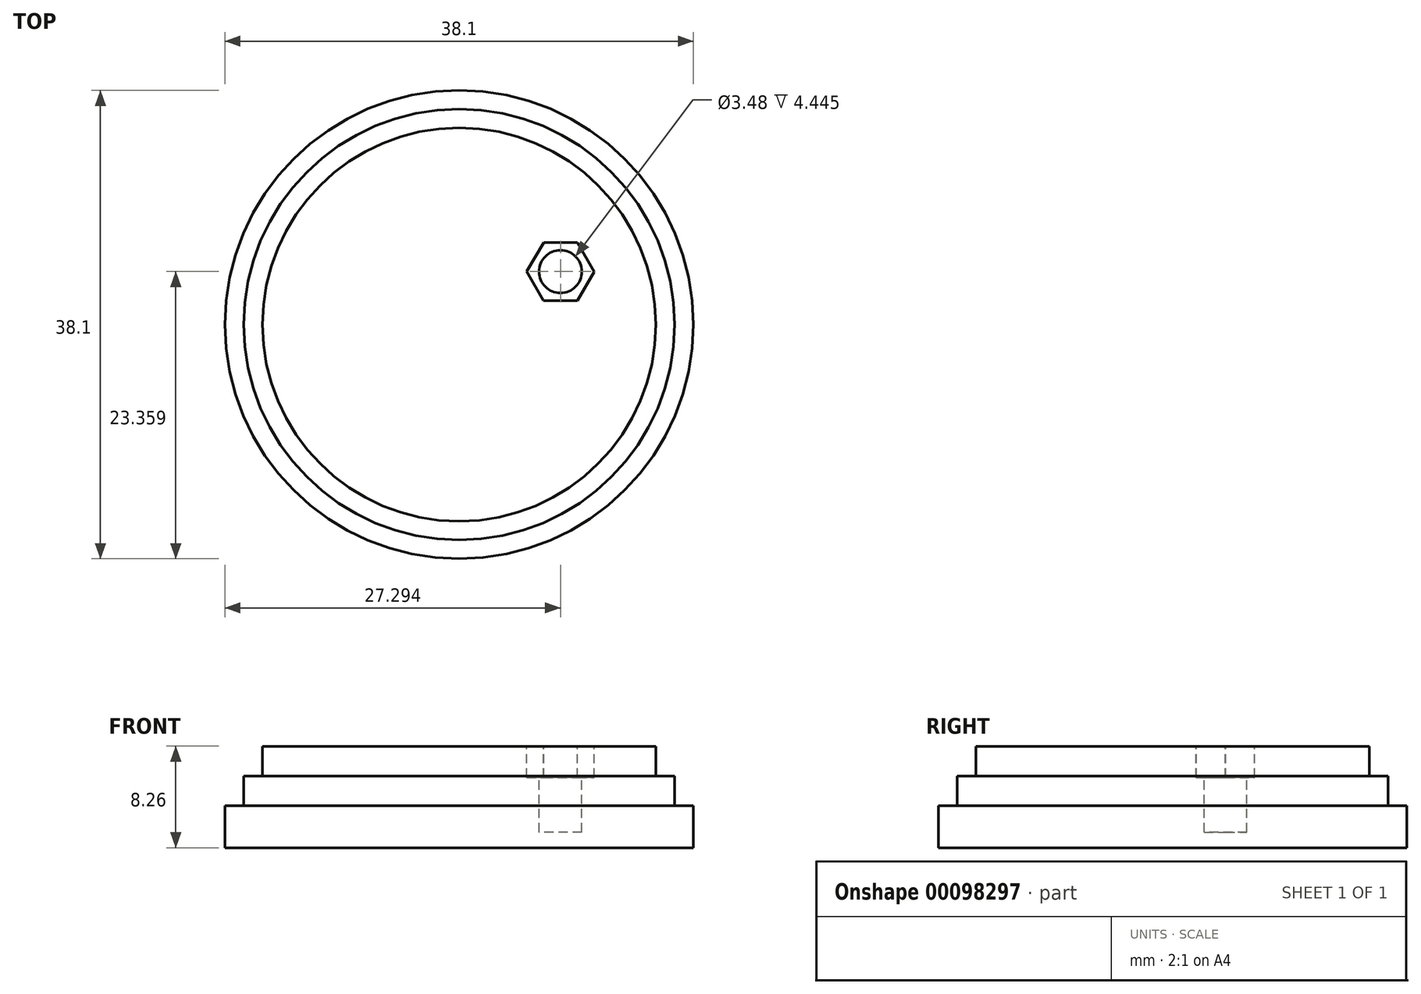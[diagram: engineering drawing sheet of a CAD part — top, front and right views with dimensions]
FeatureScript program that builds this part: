
annotation { "Feature Type Name" : "Feature", "Feature Type Description" : "" }
export const myFeature = defineFeature(function(context is Context, id is Id, definition is map)
    precondition{}
    {
        {
            var Q0;
            Q0=qCreatedBy(makeId("Front.planeOp"),FACE);
            var sketch = newSketch(context, id + "F0", { "sketchPlane" : qUnion([Q0])});
            skLineSegment(sketch, "E0", {"start": v(0, 0) * mm, "end": v(0, 3.43) * mm});
            skLineSegment(sketch, "E1", {"start": v(0, 3.43) * mm, "end": v(19.05, 3.43) * mm});
            skLineSegment(sketch, "E2", {"start": v(19.05, 3.43) * mm, "end": v(19.05, 0) * mm});
            skLineSegment(sketch, "E3", {"start": v(19.05, 0) * mm, "end": v(0, 0) * mm});
            skSolve(sketch);
        }
        {
            var Q0;
            Q0=qSketchRegion(id+"F0",true);
            var Q1;
            Q1=sQuery(id+"F0.wireOp",EDGE,"E0");
            revolve(context, id + "F1", {"entities" : qUnion([Q0]), "axis" : qUnion([Q1]), "revolveType" : RevolveType.FULL});
        }
        {
            var Q0;
            Q0=qCreatedBy(makeId("Front.planeOp"),FACE);
            var sketch = newSketch(context, id + "F2", { "sketchPlane" : qUnion([Q0])});
            skLineSegment(sketch, "E4.bottom", {"start": v(0, 3.43) * mm, "end": v(17.53, 3.43) * mm});
            skLineSegment(sketch, "E4.top", {"start": v(0, 5.84) * mm, "end": v(17.53, 5.84) * mm});
            skLineSegment(sketch, "E4.left", {"start": v(0, 3.43) * mm, "end": v(0, 5.84) * mm});
            skLineSegment(sketch, "E4.right", {"start": v(17.53, 3.43) * mm, "end": v(17.53, 5.84) * mm});
            skSolve(sketch);
        }
        {
            var Q0;
            Q0=qSketchRegion(id+"F2",true);
            var Q1;
            Q1=sQuery(id+"F2.wireOp",EDGE,"E4.left");
            revolve(context, id + "F3", {"operationType" : NewBodyOperationType.ADD, "entities" : qUnion([Q0]), "axis" : qUnion([Q1]), "revolveType" : RevolveType.FULL});
        }
        {
            var Q0;
            Q0=qCreatedBy(makeId("Front.planeOp"),FACE);
            var sketch = newSketch(context, id + "F4", { "sketchPlane" : qUnion([Q0])});
            skLineSegment(sketch, "E5.bottom", {"start": v(0, 5.84) * mm, "end": v(16, 5.84) * mm});
            skLineSegment(sketch, "E5.top", {"start": v(0, 8.25) * mm, "end": v(16, 8.25) * mm});
            skLineSegment(sketch, "E5.left", {"start": v(0, 5.84) * mm, "end": v(0, 8.25) * mm});
            skLineSegment(sketch, "E5.right", {"start": v(16, 5.84) * mm, "end": v(16, 8.25) * mm});
            skSolve(sketch);
        }
        {
            var Q0;
            Q0=qSketchRegion(id+"F4",true);
            var Q1;
            Q1=sQuery(id+"F4.wireOp",EDGE,"E5.left");
            revolve(context, id + "F5", {"operationType" : NewBodyOperationType.ADD, "entities" : qUnion([Q0]), "axis" : qUnion([Q1]), "revolveType" : RevolveType.FULL});
        }
        {
            var Q0;
            Q0=makeQuery(id+"F5.opRevolve","SWEPT_FACE",FACE,{"disambiguationData":[OSD([sQuery(id+"F4.wireOp",EDGE,"E5.top")])]});
            var sketch = newSketch(context, id + "F6", { "sketchPlane" : qUnion([Q0])});
            skCircle(sketch, "E6", {"center": v(8.24, 4.3) * mm, "radius": 1.74 * mm});
            skSolve(sketch);
        }
        {
            var Q0;
            Q0=qSketchRegion(id+"F6",true);
            extrude(context, id + "F7", {"entities" : qUnion([Q0]), "operationType" : NewBodyOperationType.REMOVE, "oppositeDirection" : true, "depth" : 7 * mm});
        }
        {
            var Q0;
            Q0=makeQuery(id+"F5.opRevolve","SWEPT_FACE",FACE,{"disambiguationData":[OSD([sQuery(id+"F4.wireOp",EDGE,"E5.top")])]});
            var sketch = newSketch(context, id + "F8", { "sketchPlane" : qUnion([Q0])});
            skCircle(sketch, "E7.cCircle", {"center": v(8.24, 4.3) * mm, "radius": 2.38 * mm, "construction": true});
            skLineSegment(sketch, "E7.0", {"start": v(9.62, 6.68) * mm, "end": v(10.99, 4.3) * mm});
            skLineSegment(sketch, "E7.1", {"start": v(10.99, 4.3) * mm, "end": v(9.61, 1.93) * mm});
            skLineSegment(sketch, "E7.2", {"start": v(9.61, 1.93) * mm, "end": v(6.87, 1.94) * mm});
            skLineSegment(sketch, "E7.3", {"start": v(6.87, 1.94) * mm, "end": v(5.5, 4.31) * mm});
            skLineSegment(sketch, "E7.4", {"start": v(5.5, 4.31) * mm, "end": v(6.88, 6.69) * mm});
            skLineSegment(sketch, "E7.5", {"start": v(6.88, 6.69) * mm, "end": v(9.62, 6.68) * mm});
            skPoint(sketch, "E7.0.midPoint", {"position": v(10.3, 5.5) * mm});
            skSolve(sketch);
        }
        {
            var Q0;
            Q0 = qSketchRegion(id + "F8", true);
            extrude(context, id + "F9", {"entities" : qUnion([Q0]), "operationType" : NewBodyOperationType.REMOVE, "oppositeDirection" : true, "depth" : 2.54 * mm});
        }
    });
